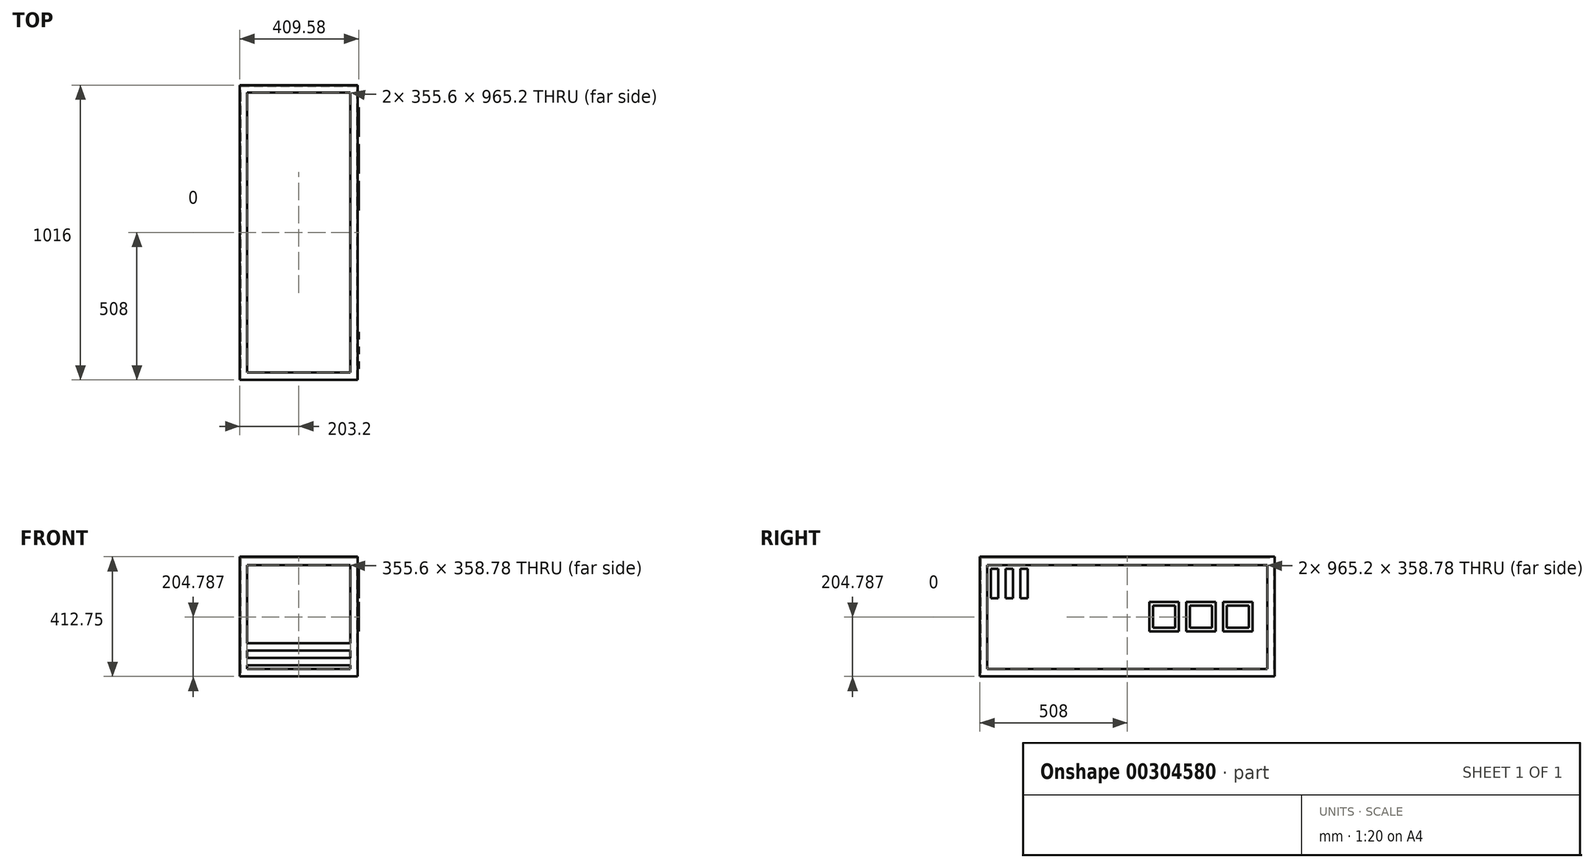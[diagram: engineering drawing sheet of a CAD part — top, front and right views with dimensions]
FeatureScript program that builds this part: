
annotation { "Feature Type Name" : "Feature", "Feature Type Description" : "" }
export const myFeature = defineFeature(function(context is Context, id is Id, definition is map)
    precondition{}
    {
        {
            var Q0;
            Q0=qCreatedBy(makeId("Top.planeOp"),FACE);
            var sketch = newSketch(context, id + "F0", { "sketchPlane" : qUnion([Q0])});
            skLineSegment(sketch, "E0.bottom", {"start": v(0, -1016) * mm, "end": v(406.4, -1016) * mm});
            skLineSegment(sketch, "E0.top", {"start": v(0, 0) * mm, "end": v(406.4, 0) * mm});
            skLineSegment(sketch, "E0.left", {"start": v(0, -1016) * mm, "end": v(0, 0) * mm});
            skLineSegment(sketch, "E0.right", {"start": v(406.4, -1016) * mm, "end": v(406.4, 0) * mm});
            skLineSegment(sketch, "E1.0", {"start": v(25.4, -990.6) * mm, "end": v(25.4, -25.4) * mm});
            skLineSegment(sketch, "E1.1", {"start": v(25.4, -990.6) * mm, "end": v(381, -990.6) * mm});
            skLineSegment(sketch, "E1.2", {"start": v(381, -990.6) * mm, "end": v(381, -25.4) * mm});
            skLineSegment(sketch, "E1.3", {"start": v(25.4, -25.4) * mm, "end": v(381, -25.4) * mm});
            skSolve(sketch);
        }
        {
            var Q0;
            Q0=makeQuery(id+"F0.imprint","IMPRINT",FACE,{"disambiguationData":[TD([[makeQuery(id+"F0.imprint","IMPRINT",EDGE,{"derivedFrom":sQuery(id+"F0.wireOp",EDGE,"E0.bottom")}),1.0]])]});
            extrude(context, id + "F1", {"entities" : qUnion([Q0]), "depth" : 3.17 * mm});
        }
        {
            var Q0;
            Q0=makeQuery(id+"F1.opExtrude","CAP_FACE",FACE,{"disambiguationData":[OSD([sQuery(id+"F0.wireOp",EDGE,"E0.bottom"),sQuery(id+"F0.wireOp",EDGE,"E0.top"),sQuery(id+"F0.wireOp",EDGE,"E0.left"),sQuery(id+"F0.wireOp",EDGE,"E0.right"),sQuery(id+"F0.wireOp",EDGE,"E1.0"),sQuery(id+"F0.wireOp",EDGE,"E1.1"),sQuery(id+"F0.wireOp",EDGE,"E1.2"),sQuery(id+"F0.wireOp",EDGE,"E1.3")])],"isStart":false});
            var sketch = newSketch(context, id + "F2", { "sketchPlane" : qUnion([Q0])});
            skLineSegment(sketch, "E2.0", {"start": v(3.18, -3.18) * mm, "end": v(403.23, -3.18) * mm});
            skLineSegment(sketch, "E2.1", {"start": v(3.18, -1012.83) * mm, "end": v(3.18, -3.17) * mm});
            skLineSegment(sketch, "E2.2", {"start": v(3.18, -1012.83) * mm, "end": v(403.23, -1012.83) * mm});
            skLineSegment(sketch, "E2.3", {"start": v(403.23, -1012.83) * mm, "end": v(403.23, -3.17) * mm});
            skSolve(sketch);
        }
        {
            var Q0;
            Q0=makeQuery(id+"F2.imprint","IMPRINT",FACE,{"disambiguationData":[TD([[makeQuery(id+"F2.imprint","IMPRINT",EDGE,{"derivedFrom":sQuery(id+"F2.wireOp",EDGE,"E2.0")}),1.0]])]});
            extrude(context, id + "F3", {"entities" : qUnion([Q0]), "operationType" : NewBodyOperationType.ADD, "depth" : 406.4 * mm});
        }
        {
            var Q0;
            {var subQ0=sQuery(id+"F0.wireOp",EDGE,"E0.right");Q0=makeQuery(id+"F3.boolean.opBoolean","MERGE",FACE,{"derivedFrom":[makeQuery(id+"F1.opExtrude","SWEPT_FACE",FACE,{"disambiguationData":[OSD([subQ0])]}),makeQuery(id+"F3.opExtrude","SWEPT_FACE",FACE,{"disambiguationData":[OSD([subQ0])]})]});}
            var sketch = newSketch(context, id + "F4", { "sketchPlane" : qUnion([Q0])});
            skLineSegment(sketch, "E3.0", {"start": v(-990.6, 25.4) * mm, "end": v(-25.4, 25.4) * mm});
            skLineSegment(sketch, "E3.1", {"start": v(-990.6, 384.18) * mm, "end": v(-990.6, 25.4) * mm});
            skLineSegment(sketch, "E3.2", {"start": v(-25.4, 384.18) * mm, "end": v(-990.6, 384.18) * mm});
            skLineSegment(sketch, "E3.3", {"start": v(-25.4, 25.4) * mm, "end": v(-25.4, 384.18) * mm});
            skSolve(sketch);
        }
        {
            var Q0;
            Q0=makeQuery(id+"F4.imprint","IMPRINT",FACE,{"disambiguationData":[TD([[makeQuery(id+"F4.imprint","IMPRINT",EDGE,{"derivedFrom":sQuery(id+"F4.wireOp",EDGE,"E3.0")}),1.0]])]});
            extrude(context, id + "F5", {"entities" : qUnion([Q0]), "operationType" : NewBodyOperationType.REMOVE, "endBound" : BoundingType.THROUGH_ALL, "oppositeDirection" : true, "depth" : 25.4 * mm});
        }
        {
            var Q0;
            {var subQ0=sQuery(id+"F0.wireOp",EDGE,"E0.bottom");Q0=makeQuery(id+"F3.boolean.opBoolean","MERGE",FACE,{"derivedFrom":[makeQuery(id+"F1.opExtrude","SWEPT_FACE",FACE,{"disambiguationData":[OSD([subQ0])]}),makeQuery(id+"F3.opExtrude","SWEPT_FACE",FACE,{"disambiguationData":[OSD([subQ0])]})]});}
            var sketch = newSketch(context, id + "F6", { "sketchPlane" : qUnion([Q0])});
            skLineSegment(sketch, "E4.0", {"start": v(25.4, 25.4) * mm, "end": v(381, 25.4) * mm});
            skLineSegment(sketch, "E4.1", {"start": v(25.4, 384.18) * mm, "end": v(25.4, 25.4) * mm});
            skLineSegment(sketch, "E4.2", {"start": v(381, 384.18) * mm, "end": v(25.4, 384.18) * mm});
            skLineSegment(sketch, "E4.3", {"start": v(381, 25.4) * mm, "end": v(381, 384.18) * mm});
            skSolve(sketch);
        }
        {
            var Q0;
            Q0=makeQuery(id+"F6.imprint","IMPRINT",FACE,{"disambiguationData":[TD([[makeQuery(id+"F6.imprint","IMPRINT",EDGE,{"derivedFrom":sQuery(id+"F6.wireOp",EDGE,"E4.0")}),1.0]])]});
            extrude(context, id + "F7", {"entities" : qUnion([Q0]), "operationType" : NewBodyOperationType.REMOVE, "endBound" : BoundingType.THROUGH_ALL, "oppositeDirection" : true, "depth" : 25.4 * mm});
        }
        {
            var Q0;
            Q0=makeQuery(id+"F3.opExtrude","CAP_FACE",FACE,{"disambiguationData":[OSD([sQuery(id+"F0.wireOp",EDGE,"E0.bottom"),sQuery(id+"F0.wireOp",EDGE,"E0.top"),sQuery(id+"F0.wireOp",EDGE,"E0.left"),sQuery(id+"F0.wireOp",EDGE,"E0.right"),sQuery(id+"F2.wireOp",EDGE,"E2.0"),sQuery(id+"F2.wireOp",EDGE,"E2.1"),sQuery(id+"F2.wireOp",EDGE,"E2.2"),sQuery(id+"F2.wireOp",EDGE,"E2.3")])],"isStart":false});
            var sketch = newSketch(context, id + "F8", { "sketchPlane" : qUnion([Q0])});
            skLineSegment(sketch, "E5.0", {"start": v(0, -1016) * mm, "end": v(0, 0) * mm});
            skLineSegment(sketch, "E6.0", {"start": v(0, 0) * mm, "end": v(406.4, 0) * mm});
            skLineSegment(sketch, "E7.0", {"start": v(406.4, -1016) * mm, "end": v(406.4, 0) * mm});
            skLineSegment(sketch, "E8.0", {"start": v(0, -1016) * mm, "end": v(406.4, -1016) * mm});
            skLineSegment(sketch, "E9.0", {"start": v(25.4, -990.6) * mm, "end": v(25.4, -25.4) * mm});
            skLineSegment(sketch, "E10.0", {"start": v(25.4, -25.4) * mm, "end": v(381, -25.4) * mm});
            skLineSegment(sketch, "E11.0", {"start": v(381, -990.6) * mm, "end": v(381, -25.4) * mm});
            skLineSegment(sketch, "E12.0", {"start": v(25.4, -990.6) * mm, "end": v(381, -990.6) * mm});
            skSolve(sketch);
        }
        {
            var Q0;
            Q0=makeQuery(id+"F8.imprint","IMPRINT",FACE,{"disambiguationData":[TD([[makeQuery(id+"F8.imprint","IMPRINT",EDGE,{"derivedFrom":sQuery(id+"F8.wireOp",EDGE,"E9.0")}),1.0]])]});
            var Q1;
            Q1=makeQuery(id+"F8.imprint","IMPRINT",FACE,{"disambiguationData":[TD([[makeQuery(id+"F8.imprint","IMPRINT",EDGE,{"derivedFrom":sQuery(id+"F8.wireOp",EDGE,"E5.0")}),-1.0]])]});
            extrude(context, id + "F9", {"entities" : qUnion([Q0, Q1]), "operationType" : NewBodyOperationType.ADD, "depth" : 3.17 * mm});
        }
        {
            var Q0;
            {var subQ0=sQuery(id+"F0.wireOp",EDGE,"E0.right");Q0=makeQuery(id+"F9.boolean.opBoolean","MERGE",FACE,{"derivedFrom":[makeQuery(id+"F3.boolean.opBoolean","MERGE",FACE,{"derivedFrom":[makeQuery(id+"F1.opExtrude","SWEPT_FACE",FACE,{"disambiguationData":[OSD([subQ0])]}),makeQuery(id+"F3.opExtrude","SWEPT_FACE",FACE,{"disambiguationData":[OSD([subQ0])]})]}),makeQuery(id+"F9.opExtrude","SWEPT_FACE",FACE,{"disambiguationData":[OSD([sQuery(id+"F8.wireOp",EDGE,"E7.0")])]})]});}
            var sketch = newSketch(context, id + "F10", { "sketchPlane" : qUnion([Q0])});
            skLineSegment(sketch, "E13", {"start": v(-1016, 206.37) * mm, "end": v(0, 206.37) * mm, "construction": true});
            skPoint(sketch, "E14", {"position": v(-127, 206.37) * mm});
            skLineSegment(sketch, "E15.bottom", {"start": v(-76.2, 155.57) * mm, "end": v(-177.8, 155.57) * mm});
            skLineSegment(sketch, "E15.top", {"start": v(-76.2, 257.17) * mm, "end": v(-177.8, 257.17) * mm});
            skLineSegment(sketch, "E15.left", {"start": v(-76.2, 155.57) * mm, "end": v(-76.2, 257.17) * mm});
            skLineSegment(sketch, "E15.right", {"start": v(-177.8, 155.57) * mm, "end": v(-177.8, 257.17) * mm});
            skLineSegment(sketch, "E16.0", {"start": v(-88.9, 244.47) * mm, "end": v(-165.1, 244.47) * mm});
            skLineSegment(sketch, "E16.1", {"start": v(-88.9, 168.27) * mm, "end": v(-88.9, 244.47) * mm});
            skLineSegment(sketch, "E16.2", {"start": v(-88.9, 168.27) * mm, "end": v(-165.1, 168.27) * mm});
            skLineSegment(sketch, "E16.3", {"start": v(-165.1, 168.27) * mm, "end": v(-165.1, 244.47) * mm});
            skLineSegment(sketch, "E17.1.0.0", {"start": v(-215.9, 168.27) * mm, "end": v(-215.9, 244.47) * mm});
            skLineSegment(sketch, "E17.1.0.1", {"start": v(-203.2, 257.17) * mm, "end": v(-304.8, 257.17) * mm});
            skLineSegment(sketch, "E17.1.0.2", {"start": v(-203.2, 155.57) * mm, "end": v(-203.2, 257.17) * mm});
            skLineSegment(sketch, "E17.1.0.3", {"start": v(-215.9, 244.47) * mm, "end": v(-292.1, 244.47) * mm});
            skLineSegment(sketch, "E17.1.0.4", {"start": v(-292.1, 168.27) * mm, "end": v(-292.1, 244.47) * mm});
            skLineSegment(sketch, "E17.1.0.5", {"start": v(-304.8, 155.57) * mm, "end": v(-304.8, 257.17) * mm});
            skLineSegment(sketch, "E17.1.0.6", {"start": v(-215.9, 168.27) * mm, "end": v(-292.1, 168.27) * mm});
            skLineSegment(sketch, "E17.1.0.7", {"start": v(-203.2, 155.57) * mm, "end": v(-304.8, 155.57) * mm});
            skLineSegment(sketch, "E17.2.0.0", {"start": v(-342.9, 168.27) * mm, "end": v(-342.9, 244.47) * mm});
            skLineSegment(sketch, "E17.2.0.1", {"start": v(-330.2, 257.17) * mm, "end": v(-431.8, 257.17) * mm});
            skLineSegment(sketch, "E17.2.0.2", {"start": v(-330.2, 155.57) * mm, "end": v(-330.2, 257.17) * mm});
            skLineSegment(sketch, "E17.2.0.3", {"start": v(-342.9, 244.47) * mm, "end": v(-419.1, 244.47) * mm});
            skLineSegment(sketch, "E17.2.0.4", {"start": v(-419.1, 168.27) * mm, "end": v(-419.1, 244.47) * mm});
            skLineSegment(sketch, "E17.2.0.5", {"start": v(-431.8, 155.57) * mm, "end": v(-431.8, 257.17) * mm});
            skLineSegment(sketch, "E17.2.0.6", {"start": v(-342.9, 168.27) * mm, "end": v(-419.1, 168.27) * mm});
            skLineSegment(sketch, "E17.2.0.7", {"start": v(-330.2, 155.57) * mm, "end": v(-431.8, 155.57) * mm});
            skLineSegment(sketch, "E17.direction1", {"start": v(-177.8, 155.57) * mm, "end": v(-304.8, 155.57) * mm, "construction": true});
            skLineSegment(sketch, "E18.0", {"start": v(-1016, 412.75) * mm, "end": v(0, 412.75) * mm});
            skLineSegment(sketch, "E18.1", {"start": v(-1016, 412.75) * mm, "end": v(-1016, 0) * mm});
            skLineSegment(sketch, "E18.2", {"start": v(0, 412.75) * mm, "end": v(0, 0) * mm});
            skLineSegment(sketch, "E18.3", {"start": v(-1016, 0) * mm, "end": v(0, 0) * mm});
            skLineSegment(sketch, "E19.bottom", {"start": v(-977.9, 371.48) * mm, "end": v(-952.5, 371.48) * mm});
            skLineSegment(sketch, "E19.top", {"start": v(-977.9, 269.88) * mm, "end": v(-952.5, 269.88) * mm});
            skLineSegment(sketch, "E19.left", {"start": v(-977.9, 371.48) * mm, "end": v(-977.9, 269.88) * mm});
            skLineSegment(sketch, "E19.right", {"start": v(-952.5, 371.48) * mm, "end": v(-952.5, 269.88) * mm});
            skLineSegment(sketch, "E20.1.0.0", {"start": v(-901.7, 371.48) * mm, "end": v(-901.7, 269.88) * mm});
            skLineSegment(sketch, "E20.1.0.1", {"start": v(-927.1, 371.48) * mm, "end": v(-927.1, 269.88) * mm});
            skLineSegment(sketch, "E20.1.0.2", {"start": v(-927.1, 371.48) * mm, "end": v(-901.7, 371.48) * mm});
            skLineSegment(sketch, "E20.1.0.3", {"start": v(-927.1, 269.88) * mm, "end": v(-901.7, 269.88) * mm});
            skLineSegment(sketch, "E20.2.0.0", {"start": v(-850.9, 371.48) * mm, "end": v(-850.9, 269.88) * mm});
            skLineSegment(sketch, "E20.2.0.1", {"start": v(-876.3, 371.48) * mm, "end": v(-876.3, 269.88) * mm});
            skLineSegment(sketch, "E20.2.0.2", {"start": v(-876.3, 371.48) * mm, "end": v(-850.9, 371.48) * mm});
            skLineSegment(sketch, "E20.2.0.3", {"start": v(-876.3, 269.88) * mm, "end": v(-850.9, 269.88) * mm});
            skLineSegment(sketch, "E20.direction1", {"start": v(-977.9, 269.88) * mm, "end": v(-927.1, 269.88) * mm, "construction": true});
            skSolve(sketch);
        }
        {
            var Q0;
            Q0=makeQuery(id+"F10.imprint","IMPRINT",FACE,{"disambiguationData":[TD([[makeQuery(id+"F10.imprint","IMPRINT",EDGE,{"derivedFrom":sQuery(id+"F10.wireOp",EDGE,"E17.1.0.0")}),-1.0]])]});
            var Q1;
            Q1=makeQuery(id+"F10.imprint","IMPRINT",FACE,{"disambiguationData":[TD([[makeQuery(id+"F10.imprint","IMPRINT",EDGE,{"derivedFrom":sQuery(id+"F10.wireOp",EDGE,"E15.bottom")}),-1.0]])]});
            var Q2;
            Q2=makeQuery(id+"F10.imprint","IMPRINT",FACE,{"disambiguationData":[TD([[makeQuery(id+"F10.imprint","IMPRINT",EDGE,{"derivedFrom":sQuery(id+"F10.wireOp",EDGE,"E17.2.0.0")}),-1.0]])]});
            var Q3;
            Q3=makeQuery(id+"F10.imprint","IMPRINT",FACE,{"disambiguationData":[TD([[makeQuery(id+"F10.imprint","IMPRINT",EDGE,{"derivedFrom":sQuery(id+"F10.wireOp",EDGE,"E20.1.0.0")}),-1.0]])]});
            var Q4;
            Q4=makeQuery(id+"F10.imprint","IMPRINT",FACE,{"disambiguationData":[TD([[makeQuery(id+"F10.imprint","IMPRINT",EDGE,{"derivedFrom":sQuery(id+"F10.wireOp",EDGE,"E19.bottom")}),-1.0]])]});
            var Q5;
            Q5=makeQuery(id+"F10.imprint","IMPRINT",FACE,{"disambiguationData":[TD([[makeQuery(id+"F10.imprint","IMPRINT",EDGE,{"derivedFrom":sQuery(id+"F10.wireOp",EDGE,"E20.2.0.0")}),-1.0]])]});
            extrude(context, id + "F11", {"entities" : qUnion([Q0, Q1, Q2, Q3, Q4, Q5]), "depth" : 3.17 * mm});
        }
        {
            var Q0;
            {var subQ0=sQuery(id+"F0.wireOp",EDGE,"E0.bottom");Q0=makeQuery(id+"F9.boolean.opBoolean","MERGE",FACE,{"derivedFrom":[makeQuery(id+"F3.boolean.opBoolean","MERGE",FACE,{"derivedFrom":[makeQuery(id+"F1.opExtrude","SWEPT_FACE",FACE,{"disambiguationData":[OSD([subQ0])]}),makeQuery(id+"F3.opExtrude","SWEPT_FACE",FACE,{"disambiguationData":[OSD([subQ0])]})]}),makeQuery(id+"F9.opExtrude","SWEPT_FACE",FACE,{"disambiguationData":[OSD([sQuery(id+"F8.wireOp",EDGE,"E8.0")])]})]});}
            var sketch = newSketch(context, id + "F12", { "sketchPlane" : qUnion([Q0])});
            skLineSegment(sketch, "E21.bottom", {"start": v(25.4, 38.1) * mm, "end": v(381, 38.1) * mm});
            skLineSegment(sketch, "E21.top", {"start": v(25.4, 63.5) * mm, "end": v(381, 63.5) * mm});
            skLineSegment(sketch, "E21.left", {"start": v(25.4, 38.1) * mm, "end": v(25.4, 63.5) * mm});
            skLineSegment(sketch, "E21.right", {"start": v(381, 38.1) * mm, "end": v(381, 63.5) * mm});
            skLineSegment(sketch, "E22.bottom", {"start": v(25.4, 88.9) * mm, "end": v(381, 88.9) * mm});
            skLineSegment(sketch, "E22.top", {"start": v(25.4, 114.3) * mm, "end": v(381, 114.3) * mm});
            skLineSegment(sketch, "E22.left", {"start": v(25.4, 88.9) * mm, "end": v(25.4, 114.3) * mm});
            skLineSegment(sketch, "E22.right", {"start": v(381, 88.9) * mm, "end": v(381, 114.3) * mm});
            skSolve(sketch);
        }
        {
            var Q0;
            Q0=makeQuery(id+"F12.imprint","IMPRINT",FACE,{"disambiguationData":[TD([[makeQuery(id+"F12.imprint","IMPRINT",EDGE,{"derivedFrom":sQuery(id+"F12.wireOp",EDGE,"E22.bottom")}),1.0]])]});
            var Q1;
            Q1=makeQuery(id+"F12.imprint","IMPRINT",FACE,{"disambiguationData":[TD([[makeQuery(id+"F12.imprint","IMPRINT",EDGE,{"derivedFrom":sQuery(id+"F12.wireOp",EDGE,"E21.bottom")}),1.0]])]});
            extrude(context, id + "F13", {"entities" : qUnion([Q0, Q1]), "operationType" : NewBodyOperationType.ADD, "oppositeDirection" : true, "depth" : 3.17 * mm});
        }
    });
